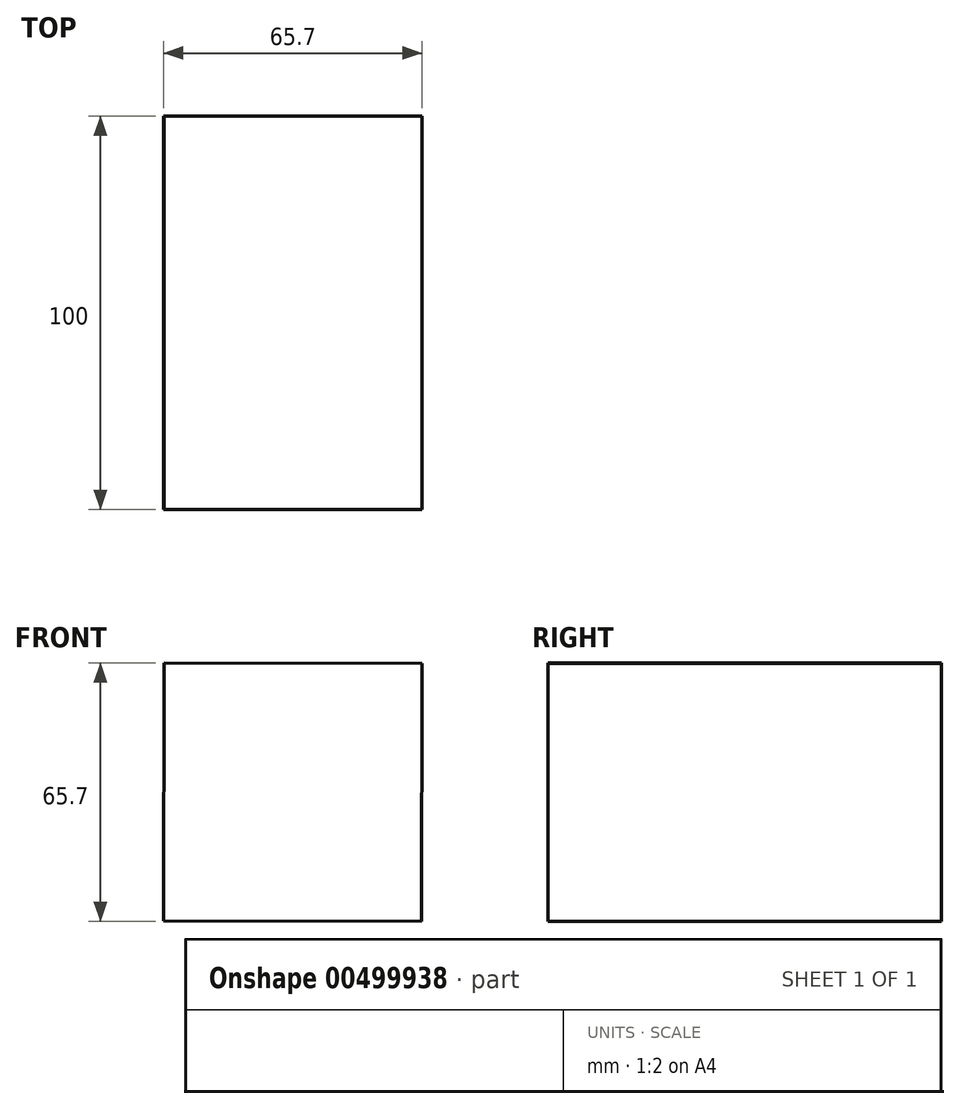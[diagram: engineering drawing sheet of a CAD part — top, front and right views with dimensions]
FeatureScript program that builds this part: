
annotation { "Feature Type Name" : "Feature", "Feature Type Description" : "" }
export const myFeature = defineFeature(function(context is Context, id is Id, definition is map)
    precondition{}
    {
        {
            var Q0;
            Q0=qCreatedBy(makeId("Front.planeOp"),FACE);
            var sketch = newSketch(context, id + "F0", { "sketchPlane" : qUnion([Q0])});
            skCircle(sketch, "E0.cCircle", {"center": v(0, 0) * mm, "radius": 46.35 * mm, "construction": true});
            skLineSegment(sketch, "E0.0", {"start": v(-32.7, 32.85) * mm, "end": v(32.85, 32.7) * mm});
            skLineSegment(sketch, "E0.1", {"start": v(32.85, 32.7) * mm, "end": v(32.7, -32.85) * mm});
            skLineSegment(sketch, "E0.2", {"start": v(32.7, -32.85) * mm, "end": v(-32.85, -32.7) * mm});
            skLineSegment(sketch, "E0.3", {"start": v(-32.85, -32.7) * mm, "end": v(-32.7, 32.85) * mm});
            skSolve(sketch);
        }
        {
            var Q0;
            Q0=makeQuery(id+"F0.imprint","IMPRINT",FACE,{"disambiguationData":[TD([[makeQuery(id+"F0.imprint","IMPRINT",EDGE,{"derivedFrom":sQuery(id+"F0.wireOp",EDGE,"E0.0")}),-1.0]])]});
            extrude(context, id + "F1", {"entities" : qUnion([Q0]), "depth" : 100 * mm});
        }
    });
